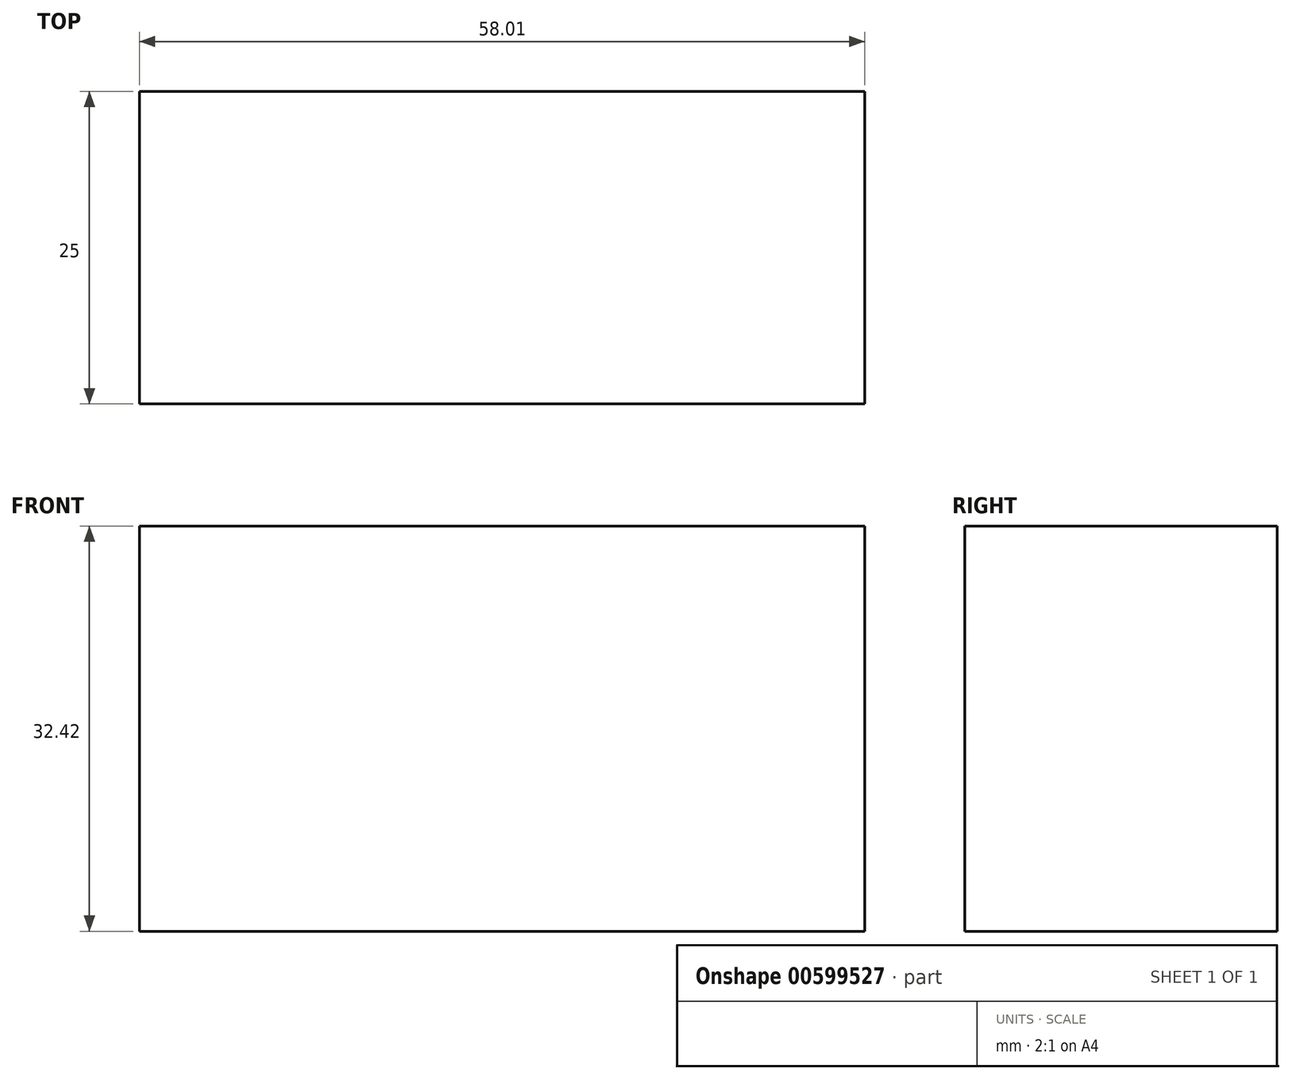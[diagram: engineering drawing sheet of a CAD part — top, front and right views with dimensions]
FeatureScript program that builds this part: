
annotation { "Feature Type Name" : "Feature", "Feature Type Description" : "" }
export const myFeature = defineFeature(function(context is Context, id is Id, definition is map)
    precondition{}
    {
        {
            var Q0;
            Q0=qCreatedBy(makeId("Front.planeOp"),FACE);
            var sketch = newSketch(context, id + "F0", { "sketchPlane" : qUnion([Q0])});
            skLineSegment(sketch, "E0.bottom", {"start": v(-30.07, 15.57) * mm, "end": v(27.94, 15.57) * mm});
            skLineSegment(sketch, "E0.top", {"start": v(-30.07, -16.85) * mm, "end": v(27.94, -16.85) * mm});
            skLineSegment(sketch, "E0.left", {"start": v(-30.07, 15.57) * mm, "end": v(-30.07, -16.85) * mm});
            skLineSegment(sketch, "E0.right", {"start": v(27.94, 15.57) * mm, "end": v(27.94, -16.85) * mm});
            skSolve(sketch);
        }
        {
            var Q0;
            Q0 = qSketchRegion(id + "F0", true);
            extrude(context, id + "F1", {"entities" : qUnion([Q0]), "depth" : 25 * mm, "offsetDistance" : 25 * mm});
        }
    });
